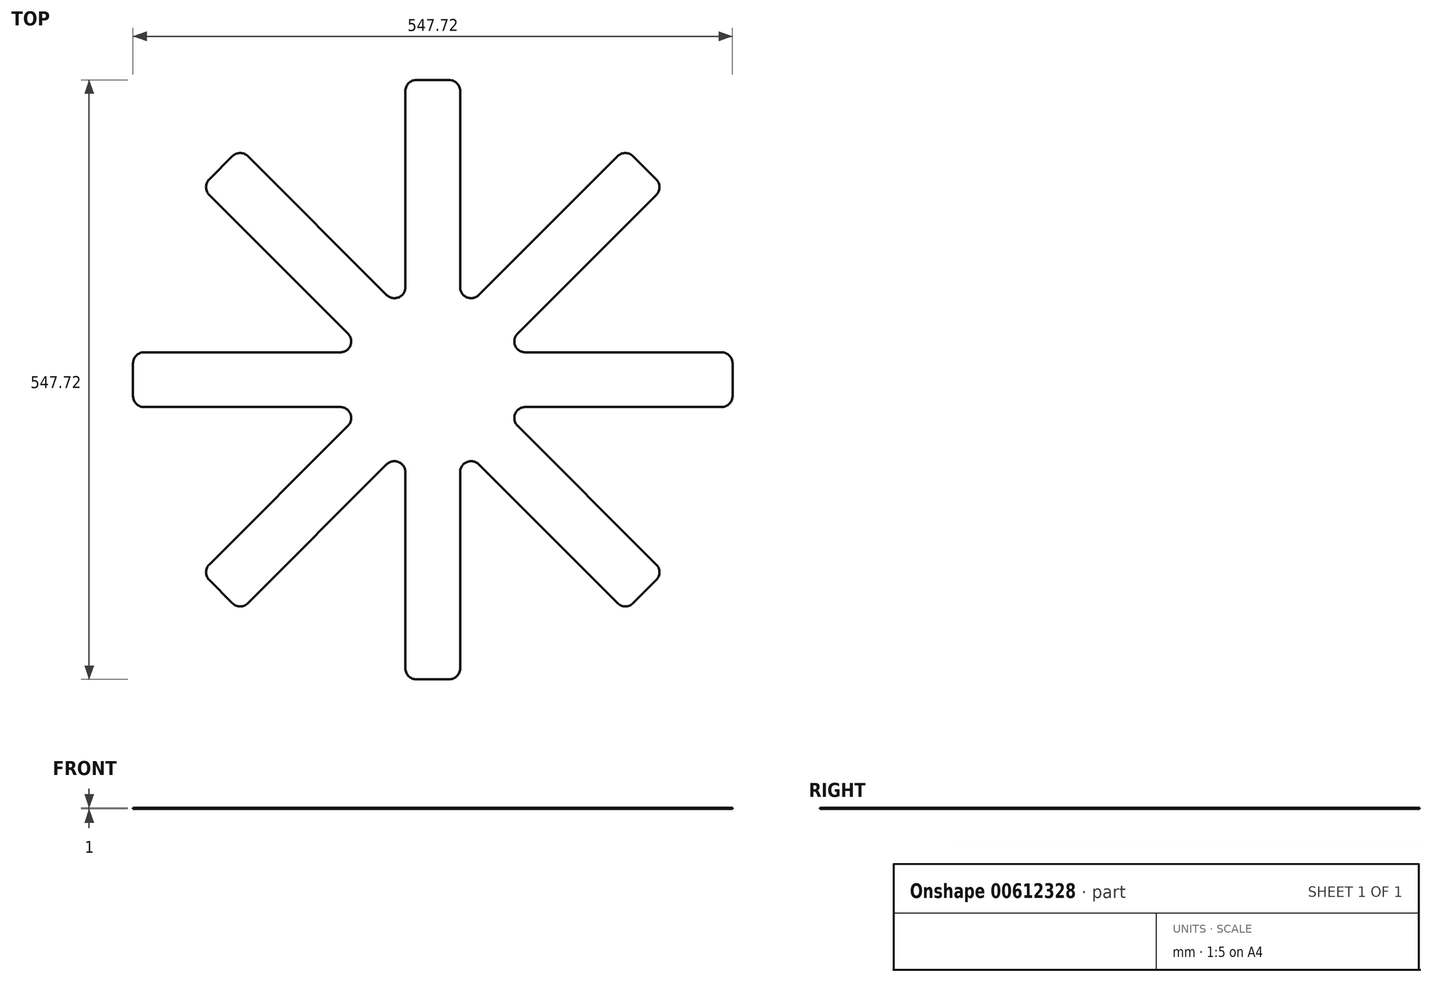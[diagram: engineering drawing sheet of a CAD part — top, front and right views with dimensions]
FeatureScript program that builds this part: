
annotation { "Feature Type Name" : "Feature", "Feature Type Description" : "" }
export const myFeature = defineFeature(function(context is Context, id is Id, definition is map)
    precondition{}
    {
        {
            var Q0;
            Q0=qCreatedBy(makeId("Top.planeOp"),FACE);
            var sketch = newSketch(context, id + "F0", { "sketchPlane" : qUnion([Q0])});
            skCircle(sketch, "E0", {"center": v(0, 0) * mm, "radius": 64 * mm});
            skSolve(sketch);
        }
        {
            var Q0;
            Q0 = qSketchRegion(id + "F0", true);
            extrude(context, id + "F1", {"entities" : qUnion([Q0]), "depth" : 1 * mm, "offsetDistance" : 25 * mm});
        }
        {
            var Q0;
            Q0=qCreatedBy(makeId("Top.planeOp"),FACE);
            var sketch = newSketch(context, id + "F2", { "sketchPlane" : qUnion([Q0])});
            skCircle(sketch, "E1", {"center": v(0, 0) * mm, "radius": 275 * mm});
            skLineSegment(sketch, "E2.bottom", {"start": v(-25, 58.92) * mm, "end": v(25, 58.92) * mm});
            skLineSegment(sketch, "E2.top", {"start": v(-25, 273.86) * mm, "end": v(25, 273.86) * mm});
            skLineSegment(sketch, "E2.left", {"start": v(-25, 58.92) * mm, "end": v(-25, 273.86) * mm});
            skLineSegment(sketch, "E2.right", {"start": v(25, 58.92) * mm, "end": v(25, 273.86) * mm});
            skPoint(sketch, "E3", {"position": v(0, 58.92) * mm});
            skSolve(sketch);
        }
        {
            var Q0;
            Q0=makeQuery(id+"F2.imprint","IMPRINT",FACE,{"disambiguationData":[TD([[makeQuery(id+"F2.imprint","IMPRINT",EDGE,{"derivedFrom":sQuery(id+"F2.wireOp",EDGE,"E2.bottom")}),1.0]])]});
            extrude(context, id + "F3", {"entities" : qUnion([Q0]), "operationType" : NewBodyOperationType.ADD, "depth" : 1 * mm, "offsetDistance" : 25 * mm});
        }
        {
            var Q0;
            Q0=makeQuery(id+"F3.opExtrude","SWEPT_EDGE",EDGE,{"disambiguationData":[OSD([sQuery(id+"F2.wireOp",EDGE,"E1"),sQuery(id+"F2.wireOp",EDGE,"E2.top"),sQuery(id+"F2.wireOp",EDGE,"E2.left")])]});
            var Q1;
            Q1=makeQuery(id+"F3.opExtrude","SWEPT_EDGE",EDGE,{"disambiguationData":[OSD([sQuery(id+"F2.wireOp",EDGE,"E1"),sQuery(id+"F2.wireOp",EDGE,"E2.top"),sQuery(id+"F2.wireOp",EDGE,"E2.right")])]});
            fillet(context, id + "F4", {"entities" : qUnion([Q0, Q1]), "radius" : 10 * mm, "tangentPropagation" : true, "allowEdgeOverflow" : false});
        }
        {
            var Q0;
            Q0=makeQuery(id+"F1.opExtrude","SWEPT_BODY",BODY,{"disambiguationData":[OSD([sQuery(id+"F0.wireOp",EDGE,"E0")])]});
            var Q1;
            Q1=makeQuery(id+"F1.opExtrude","CAP_EDGE",EDGE,{"disambiguationData":[OSD([sQuery(id+"F0.wireOp",EDGE,"E0")])],"isStart":true});
            circularPattern(context, id + "F5", {"operationType" : NewBodyOperationType.ADD, "entities" : qUnion([Q0]), "axis" : qUnion([Q1]), "angle" : 360 * degree, "instanceCount" : 8, "equalSpace" : true});
        }
        {
            var Q0;
            Q0=makeQuery(id+"F5.boolean.opBoolean","INTERSECT",EDGE,{"derivedFrom":[makeQuery(id+"F5.opPattern","COPY",FACE,{"derivedFrom":makeQuery(id+"F3.opExtrude","SWEPT_FACE",FACE,{"disambiguationData":[OSD([sQuery(id+"F2.wireOp",EDGE,"E2.left")])]}),"instanceName":"4"}),makeQuery(id+"F5.opPattern","COPY",FACE,{"derivedFrom":makeQuery(id+"F3.opExtrude","SWEPT_FACE",FACE,{"disambiguationData":[OSD([sQuery(id+"F2.wireOp",EDGE,"E2.right")])]}),"instanceName":"5"})]});
            var Q1;
            Q1=makeQuery(id+"F5.boolean.opBoolean","INTERSECT",EDGE,{"derivedFrom":[makeQuery(id+"F3.opExtrude","SWEPT_FACE",FACE,{"disambiguationData":[OSD([sQuery(id+"F2.wireOp",EDGE,"E2.right")])]}),makeQuery(id+"F5.opPattern","COPY",FACE,{"derivedFrom":makeQuery(id+"F3.opExtrude","SWEPT_FACE",FACE,{"disambiguationData":[OSD([sQuery(id+"F2.wireOp",EDGE,"E2.left")])]}),"instanceName":"7"})]});
            var Q2;
            Q2=makeQuery(id+"F5.boolean.opBoolean","INTERSECT",EDGE,{"derivedFrom":[makeQuery(id+"F3.opExtrude","SWEPT_FACE",FACE,{"disambiguationData":[OSD([sQuery(id+"F2.wireOp",EDGE,"E2.left")])]}),makeQuery(id+"F5.opPattern","COPY",FACE,{"derivedFrom":makeQuery(id+"F3.opExtrude","SWEPT_FACE",FACE,{"disambiguationData":[OSD([sQuery(id+"F2.wireOp",EDGE,"E2.right")])]}),"instanceName":"1"})]});
            var Q3;
            Q3=makeQuery(id+"F5.boolean.opBoolean","INTERSECT",EDGE,{"derivedFrom":[makeQuery(id+"F5.opPattern","COPY",FACE,{"derivedFrom":makeQuery(id+"F3.opExtrude","SWEPT_FACE",FACE,{"disambiguationData":[OSD([sQuery(id+"F2.wireOp",EDGE,"E2.left")])]}),"instanceName":"3"}),makeQuery(id+"F5.opPattern","COPY",FACE,{"derivedFrom":makeQuery(id+"F3.opExtrude","SWEPT_FACE",FACE,{"disambiguationData":[OSD([sQuery(id+"F2.wireOp",EDGE,"E2.right")])]}),"instanceName":"4"})]});
            var Q4;
            Q4=makeQuery(id+"F5.boolean.opBoolean","INTERSECT",EDGE,{"derivedFrom":[makeQuery(id+"F5.opPattern","COPY",FACE,{"derivedFrom":makeQuery(id+"F3.opExtrude","SWEPT_FACE",FACE,{"disambiguationData":[OSD([sQuery(id+"F2.wireOp",EDGE,"E2.left")])]}),"instanceName":"5"}),makeQuery(id+"F5.opPattern","COPY",FACE,{"derivedFrom":makeQuery(id+"F3.opExtrude","SWEPT_FACE",FACE,{"disambiguationData":[OSD([sQuery(id+"F2.wireOp",EDGE,"E2.right")])]}),"instanceName":"6"})]});
            var Q5;
            Q5=makeQuery(id+"F5.boolean.opBoolean","INTERSECT",EDGE,{"derivedFrom":[makeQuery(id+"F5.opPattern","COPY",FACE,{"derivedFrom":makeQuery(id+"F3.opExtrude","SWEPT_FACE",FACE,{"disambiguationData":[OSD([sQuery(id+"F2.wireOp",EDGE,"E2.left")])]}),"instanceName":"6"}),makeQuery(id+"F5.opPattern","COPY",FACE,{"derivedFrom":makeQuery(id+"F3.opExtrude","SWEPT_FACE",FACE,{"disambiguationData":[OSD([sQuery(id+"F2.wireOp",EDGE,"E2.right")])]}),"instanceName":"7"})]});
            var Q6;
            Q6=makeQuery(id+"F5.boolean.opBoolean","INTERSECT",EDGE,{"derivedFrom":[makeQuery(id+"F5.opPattern","COPY",FACE,{"derivedFrom":makeQuery(id+"F3.opExtrude","SWEPT_FACE",FACE,{"disambiguationData":[OSD([sQuery(id+"F2.wireOp",EDGE,"E2.left")])]}),"instanceName":"2"}),makeQuery(id+"F5.opPattern","COPY",FACE,{"derivedFrom":makeQuery(id+"F3.opExtrude","SWEPT_FACE",FACE,{"disambiguationData":[OSD([sQuery(id+"F2.wireOp",EDGE,"E2.right")])]}),"instanceName":"3"})]});
            var Q7;
            Q7=makeQuery(id+"F5.boolean.opBoolean","INTERSECT",EDGE,{"derivedFrom":[makeQuery(id+"F5.opPattern","COPY",FACE,{"derivedFrom":makeQuery(id+"F3.opExtrude","SWEPT_FACE",FACE,{"disambiguationData":[OSD([sQuery(id+"F2.wireOp",EDGE,"E2.left")])]}),"instanceName":"1"}),makeQuery(id+"F5.opPattern","COPY",FACE,{"derivedFrom":makeQuery(id+"F3.opExtrude","SWEPT_FACE",FACE,{"disambiguationData":[OSD([sQuery(id+"F2.wireOp",EDGE,"E2.right")])]}),"instanceName":"2"})]});
            fillet(context, id + "F6", {"entities" : qUnion([Q0, Q1, Q2, Q3, Q4, Q5, Q6, Q7]), "radius" : 10 * mm, "tangentPropagation" : true, "allowEdgeOverflow" : false});
        }
    });
